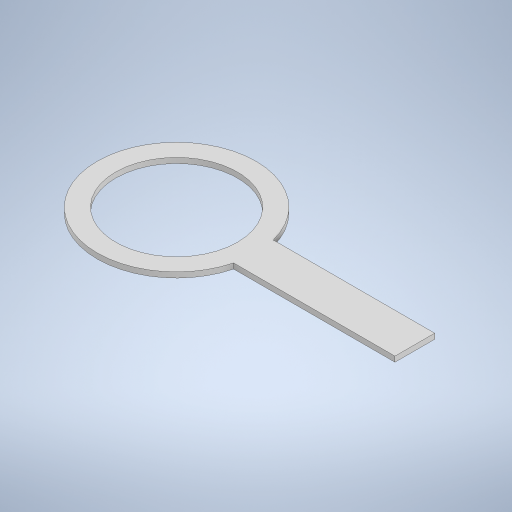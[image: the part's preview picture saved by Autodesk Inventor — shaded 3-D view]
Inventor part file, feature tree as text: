
AUTODESK INVENTOR PART (.ipt)
format: ipt  version: 2024 (Build 280153000, 153)  size: 242,176 bytes
history: native  units: mm
features: other x1, extrude x1, sketch x1
ambient origin geometry x8: Origin, YZ Plane, XZ Plane, XY Plane, X Axis, Y Axis, Z Axis, Center Point
bodies: Body1 (feature_tree)
feature tree (3):
  other  "솔리드1"
  extrude  "돌출1"  Depth=30.0mm
  sketch  "스케치1"
